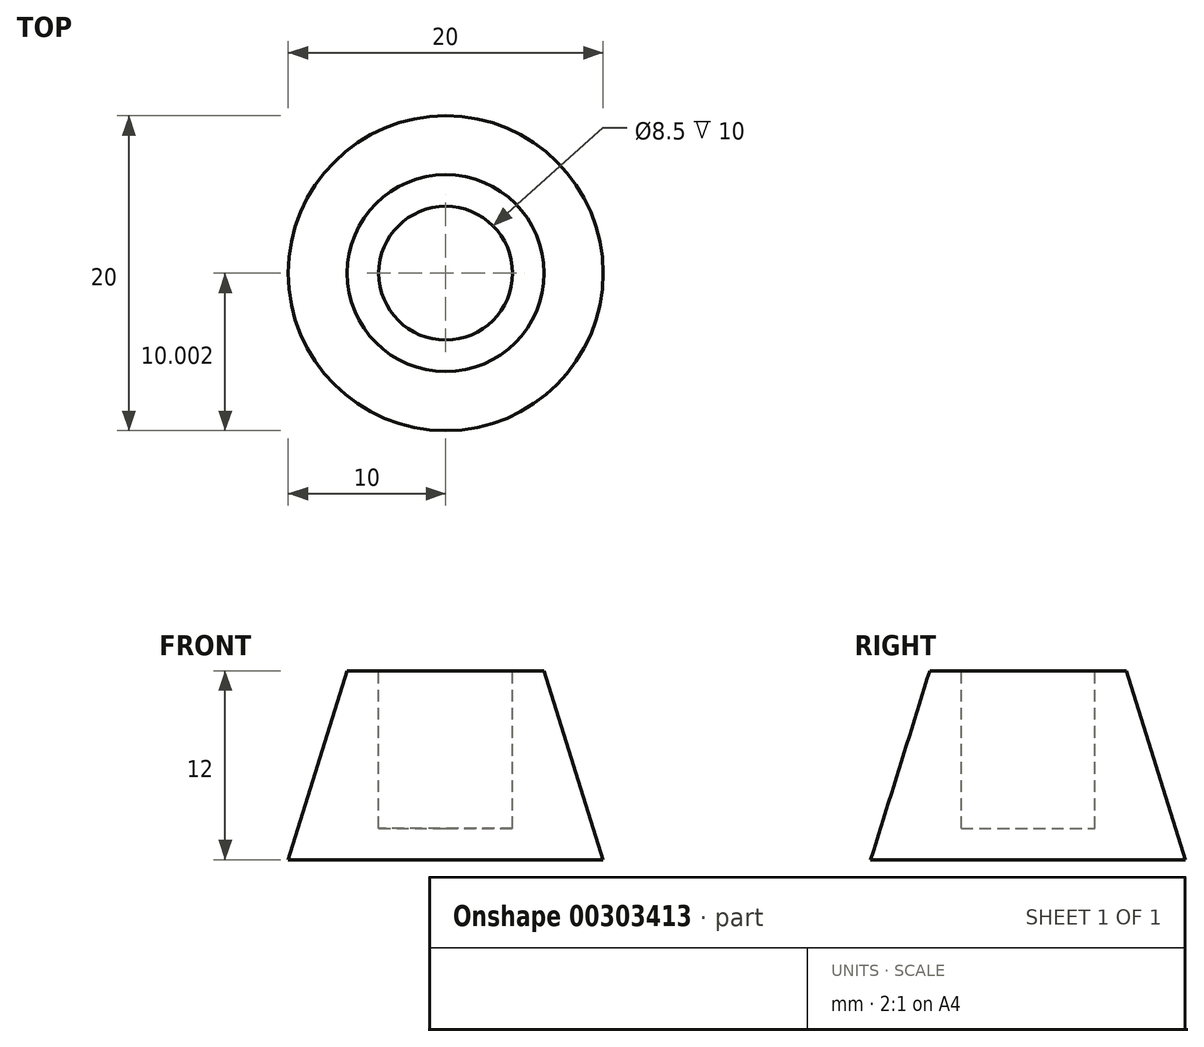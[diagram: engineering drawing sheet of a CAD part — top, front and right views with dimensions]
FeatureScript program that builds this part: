
annotation { "Feature Type Name" : "Feature", "Feature Type Description" : "" }
export const myFeature = defineFeature(function(context is Context, id is Id, definition is map)
    precondition{}
    {
        {
            var Q0;
            Q0=qCreatedBy(makeId("Right.planeOp"),FACE);
            var sketch = newSketch(context, id + "F0", { "sketchPlane" : qUnion([Q0])});
            skLineSegment(sketch, "E0", {"start": v(-3.38, -4.93) * mm, "end": v(0.87, -4.93) * mm});
            skLineSegment(sketch, "E1", {"start": v(0.87, -4.93) * mm, "end": v(0.87, -6.93) * mm});
            skLineSegment(sketch, "E2", {"start": v(0.87, -6.93) * mm, "end": v(-9.13, -6.93) * mm});
            skLineSegment(sketch, "E3", {"start": v(-3.38, -4.93) * mm, "end": v(-3.38, 5.07) * mm});
            skLineSegment(sketch, "E4", {"start": v(-3.38, 5.07) * mm, "end": v(-5.38, 5.07) * mm});
            skFitSpline(sketch, "E5", {"points": [v(-5.38, 5.07) * mm, v(-9.13, -6.93) * mm], "startDerivative": vector(-3.75, -12) * mm, "endDerivative": vector(-3.75, -12) * mm});
            skSolve(sketch);
        }
        {
            var Q0;
            Q0=makeQuery(id+"F0.imprint","IMPRINT",FACE,{"disambiguationData":[TD([[makeQuery(id+"F0.imprint","IMPRINT",EDGE,{"derivedFrom":sQuery(id+"F0.wireOp",EDGE,"E0")}),-1.0]])]});
            var Q1;
            Q1=sQuery(id+"F0.wireOp",EDGE,"E1");
            revolve(context, id + "F1", {"entities" : qUnion([Q0]), "axis" : qUnion([Q1]), "revolveType" : RevolveType.FULL});
        }
    });
